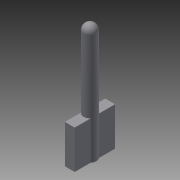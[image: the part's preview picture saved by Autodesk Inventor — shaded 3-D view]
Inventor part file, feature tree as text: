
AUTODESK INVENTOR PART (.ipt)
format: ipt  version: 2015 (Build 190159000, 159)  size: 88,064 bytes
history: native  units: in
note: dims shown in document units (in); Inventor stores cm internally (conversion verified against a paired STEP export)
features: extrude x2, sketch x1, fillet x1
ambient origin geometry x8: Origin, YZ Plane, XZ Plane, XY Plane, X Axis, Y Axis, Z Axis, Center Point
bodies: Solid1 (feature_tree)
feature tree (4):
  sketch  "Sketch1"  dims[d0=0.78in d1=0.19in d2=0.25in d3=0.39in d4=0.095in d5=0.74in d6=0.0in d7=2.25in d8=0.0in d9=0.125in]
  extrude  "Extrusion1"  Depth=0.19in
  extrude  "Extrusion2"  Depth=0.125in
  fillet  "Fillet1"  Radius=0.095in
